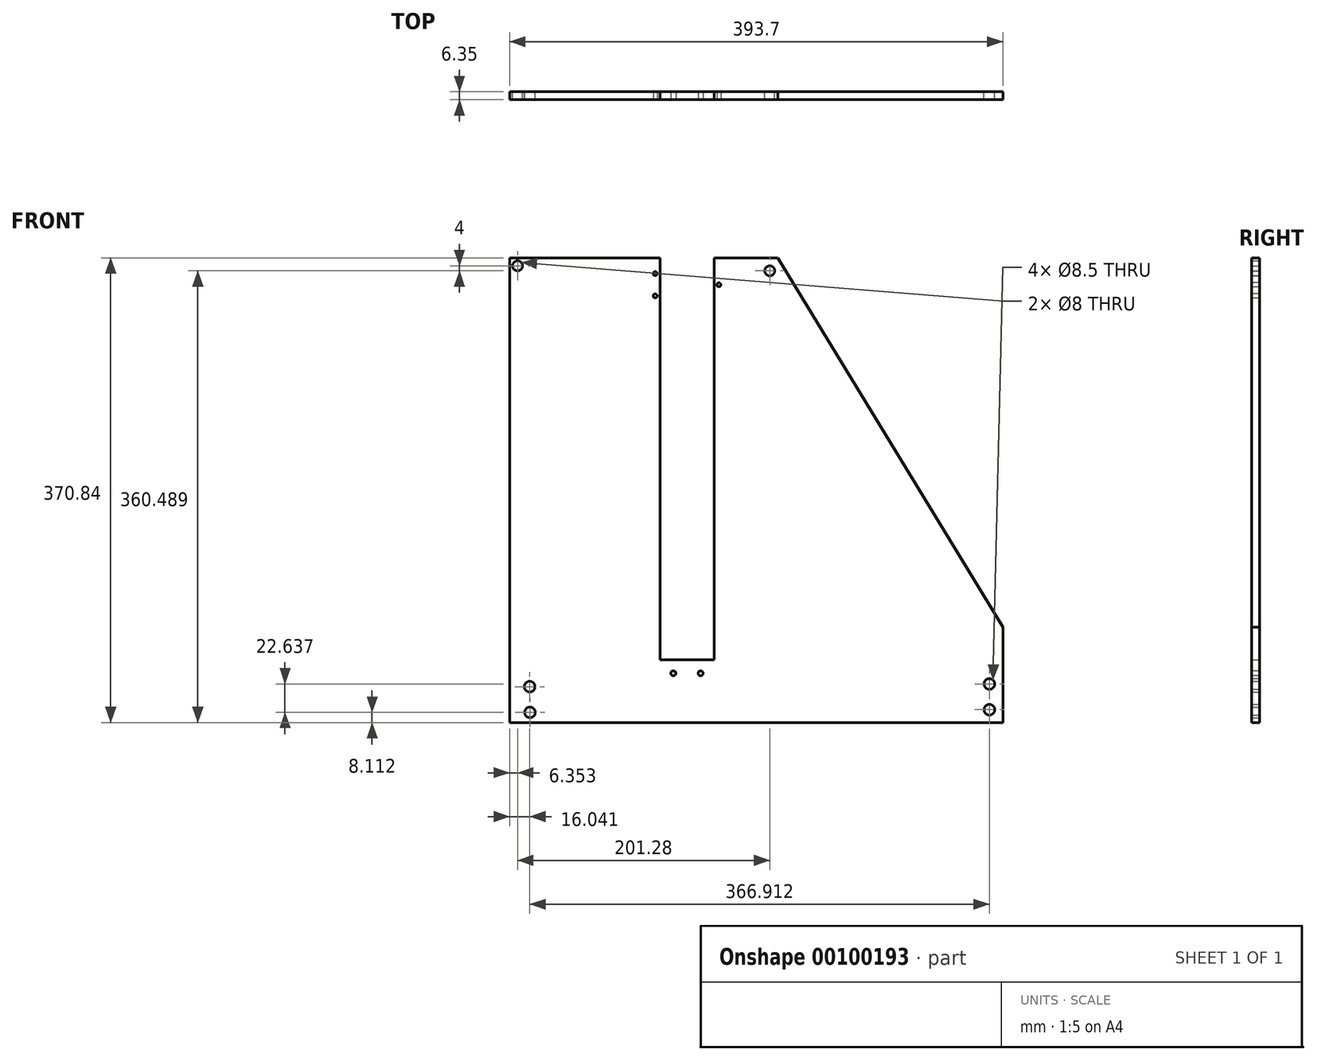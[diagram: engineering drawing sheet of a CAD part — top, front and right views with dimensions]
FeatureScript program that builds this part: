
annotation { "Feature Type Name" : "Feature", "Feature Type Description" : "" }
export const myFeature = defineFeature(function(context is Context, id is Id, definition is map)
    precondition{}
    {
        {
            var Q0;
            Q0=qCreatedBy(makeId("Front.planeOp"),FACE);
            var sketch = newSketch(context, id + "F0", { "sketchPlane" : qUnion([Q0])});
            skLineSegment(sketch, "E0.bottom", {"start": v(-199.67, -123.71) * mm, "end": v(194.03, -123.71) * mm});
            skLineSegment(sketch, "E0.top", {"start": v(-199.67, 247.13) * mm, "end": v(-79.67, 247.13) * mm});
            skLineSegment(sketch, "E0.left", {"start": v(-199.67, -123.71) * mm, "end": v(-199.67, 247.13) * mm});
            skLineSegment(sketch, "E0.right", {"start": v(194.03, -123.71) * mm, "end": v(194.03, -47.51) * mm});
            skPoint(sketch, "E1", {"position": v(-79.67, 247.13) * mm});
            skPoint(sketch, "E2", {"position": v(-36.49, 247.13) * mm});
            skPoint(sketch, "E3", {"position": v(194.03, -47.51) * mm});
            skLineSegment(sketch, "E4", {"start": v(-36.49, 247.13) * mm, "end": v(-36.49, -73.71) * mm, "construction": true});
            skPoint(sketch, "E5", {"position": v(-79.67, -91.71) * mm});
            skLineSegment(sketch, "E6", {"start": v(-36.49, -73.71) * mm, "end": v(-36.49, 247.13) * mm});
            skLineSegment(sketch, "E7", {"start": v(-79.67, -73.71) * mm, "end": v(-79.67, 247.13) * mm});
            skLineSegment(sketch, "E8.trimOffspring", {"start": v(-36.49, 247.13) * mm, "end": v(14.31, 247.13) * mm});
            skLineSegment(sketch, "E9", {"start": v(14.31, 247.13) * mm, "end": v(194.03, -47.51) * mm});
            skPoint(sketch, "E10.orphan", {"position": v(-79.67, -123.71) * mm});
            skLineSegment(sketch, "E11", {"start": v(-36.49, -73.71) * mm, "end": v(-79.67, -73.71) * mm});
            skPoint(sketch, "E12", {"position": v(194.03, -117.71) * mm});
            skPoint(sketch, "E13", {"position": v(194.03, -105.71) * mm});
            skLineSegment(sketch, "E14.0", {"start": v(172.03, -123.71) * mm, "end": v(172.03, -73.71) * mm, "construction": true});
            skCircle(sketch, "E15", {"center": v(183.28, -92.96) * mm, "radius": 4.25 * mm});
            skCircle(sketch, "E16", {"center": v(183.28, -113.46) * mm, "radius": 4.25 * mm});
            skPoint(sketch, "E17", {"position": v(172.03, -73.71) * mm});
            skLineSegment(sketch, "E18", {"start": v(172.03, -73.71) * mm, "end": v(194.03, -73.71) * mm, "construction": true});
            skLineSegment(sketch, "E19", {"start": v(0, -123.71) * mm, "end": v(-2.82, 359.54) * mm, "construction": true});
            skPoint(sketch, "E19.endSnap0", {"position": v(-2.82, -123.71) * mm});
            skCircle(sketch, "E20.MirrorC", {"center": v(-183.39, -115.6) * mm, "radius": 4.25 * mm});
            skCircle(sketch, "E21.MirrorC", {"center": v(-183.63, -95.1) * mm, "radius": 4.25 * mm});
            skCircle(sketch, "E22", {"center": v(-193.32, 240.78) * mm, "radius": 4 * mm});
            skCircle(sketch, "E23", {"center": v(7.96, 236.78) * mm, "radius": 4 * mm});
            skPoint(sketch, "E24", {"position": v(-48.5, 225.54) * mm});
            skSolve(sketch);
        }
        {
            var Q0;
            Q0=makeQuery(id+"F0.imprint","IMPRINT",FACE,{"disambiguationData":[TD([[makeQuery(id+"F0.imprint","IMPRINT",EDGE,{"derivedFrom":sQuery(id+"F0.wireOp",EDGE,"E0.bottom")}),1.0]])]});
            extrude(context, id + "F1", {"entities" : qUnion([Q0]), "depth" : 6.35 * mm});
        }
        {
            var Q0;
            Q0=makeQuery(id+"F1.opExtrude","CAP_FACE",FACE,{"disambiguationData":[OSD([sQuery(id+"F0.wireOp",EDGE,"E0.bottom"),sQuery(id+"F0.wireOp",EDGE,"E0.top"),sQuery(id+"F0.wireOp",EDGE,"E0.left"),sQuery(id+"F0.wireOp",EDGE,"E0.right"),sQuery(id+"F0.wireOp",EDGE,"E6"),sQuery(id+"F0.wireOp",EDGE,"E7"),sQuery(id+"F0.wireOp",EDGE,"E8.trimOffspring"),sQuery(id+"F0.wireOp",EDGE,"E9"),sQuery(id+"F0.wireOp",EDGE,"E11")])],"isStart":false});
            var sketch = newSketch(context, id + "F2", { "sketchPlane" : qUnion([Q0])});
            skSolve(sketch);
        }
        {
            var Q0;
            Q0=makeQuery(id+"F2.imprint","IMPRINT",FACE,{"disambiguationData":[TD([[makeQuery(id+"F2.imprint","IMPRINT",EDGE,{"derivedFrom":makeQuery(id+"F1.opExtrude","CAP_EDGE",EDGE,{"disambiguationData":[OSD([sQuery(id+"F0.wireOp",EDGE,"E0.bottom")])],"isStart":false})}),1.0]])]});
            var sketch = newSketch(context, id + "F3", { "sketchPlane" : qUnion([Q0])});
            skCircle(sketch, "E25", {"center": v(-32.68, 225.6) * mm, "radius": 1.6 * mm});
            skCircle(sketch, "E26", {"center": v(-83.48, 234.5) * mm, "radius": 1.6 * mm});
            skCircle(sketch, "E27", {"center": v(-83.48, 216.72) * mm, "radius": 1.6 * mm});
            skLineSegment(sketch, "E28", {"start": v(-83.48, 234.5) * mm, "end": v(-83.48, 216.72) * mm, "construction": true});
            skLineSegment(sketch, "E29", {"start": v(86.25, 225.6) * mm, "end": v(-83.48, 225.6) * mm, "construction": true});
            skPoint(sketch, "E30", {"position": v(129.27, 225.6) * mm});
            skLineSegment(sketch, "E31", {"start": v(129.27, 225.6) * mm, "end": v(85.4, 225.6) * mm, "construction": true});
            skLineSegment(sketch, "E32.top", {"start": v(-28.87, 204.02) * mm, "end": v(-87.29, 204.02) * mm, "construction": true});
            skLineSegment(sketch, "E32.left", {"start": v(-28.87, 247.2) * mm, "end": v(-28.87, 204.02) * mm, "construction": true});
            skLineSegment(sketch, "E32.right", {"start": v(-87.29, 247.2) * mm, "end": v(-87.29, 204.02) * mm, "construction": true});
            skLineSegment(sketch, "E33", {"start": v(-87.29, 247.2) * mm, "end": v(-28.87, 247.2) * mm, "construction": true});
            skLineSegment(sketch, "E34", {"start": v(-79.67, -99.11) * mm, "end": v(-79.67, -73.71) * mm, "construction": true});
            skLineSegment(sketch, "E35", {"start": v(-79.67, -73.71) * mm, "end": v(-36.49, -73.71) * mm, "construction": true});
            skLineSegment(sketch, "E36", {"start": v(-36.49, -73.71) * mm, "end": v(-36.49, -99.11) * mm, "construction": true});
            skLineSegment(sketch, "E37", {"start": v(-36.49, -99.11) * mm, "end": v(-79.67, -99.11) * mm, "construction": true});
            skCircle(sketch, "E38", {"center": v(-68.97, -84.41) * mm, "radius": 2 * mm});
            skCircle(sketch, "E39", {"center": v(-47.19, -84.41) * mm, "radius": 2 * mm});
            skLineSegment(sketch, "E40.0", {"start": v(-79.67, -73.71) * mm, "end": v(-79.67, 247.13) * mm, "construction": true});
            skLineSegment(sketch, "E41", {"start": v(-79.67, -73.71) * mm, "end": v(-31.5, -73.71) * mm, "construction": true});
            skSolve(sketch);
        }
        {
            var Q0;
            Q0 = qSketchRegion(id + "F3", true);
            extrude(context, id + "F4", {"entities" : qUnion([Q0]), "operationType" : NewBodyOperationType.REMOVE, "oppositeDirection" : true, "depth" : 25.4 * mm});
        }
    });
